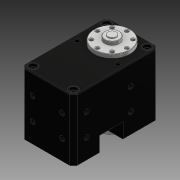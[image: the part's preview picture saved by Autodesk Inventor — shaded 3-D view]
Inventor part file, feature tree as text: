
AUTODESK INVENTOR PART (.ipt)
format: ipt  version: 2016 (Build 200138000, 138)  size: 858,624 bytes
history: native  units: mm
features: other x22, extrude x2, sketch x2
ambient origin geometry x8: Origin, YZ Plane, XZ Plane, XY Plane, X Axis, Y Axis, Z Axis, Center Point
bodies: Body1 (feature_tree), Body2 (feature_tree), Body3 (feature_tree), Body4 (feature_tree), Body5 (feature_tree), Body6 (feature_tree), Body7 (feature_tree), Body8 (feature_tree), Body9 (feature_tree)
feature tree (26):
  other  "<userpath>\Dropbox\Snake\SnakeRobot_normal\cad\parameter_base.xlsx"
  other  "ソリッド1"
  other  "作業平面1"
  extrude  "押し出し1"  Depth=0.5mm
  extrude  "押し出し2"  Depth=10.0mm TaperAngle=0.0deg
  other  "ソリッド2"
  other  "ソリッド3"
  other  "ソリッド4"
  other  "ソリッド5"
  other  "ソリッド6"
  other  "ソリッド7"
  other  "ソリッド8"
  other  "ソリッド9"
  other  "ソリッド10"
  sketch  "スケッチ1"
  sketch  "スケッチ2"
  other  "X-430_IDLE_10:1"
  other  "X-430_SPACER_RING_11:1"
  other  "X-430_SPACER_RING_12:1"
  other  "X-430_SPACER_RING_13:1"
  other  "X-430_SPACER_RING_14:1"
  other  "X-430_SPACER_RING_15:1"
  other  "X-430_SPACER_RING_16:1"
  other  "X-430_SPACER_RING_17:1"
  other  "X-430_SPACER_RING_18:1"
  other  "X-430_CVR_CABLE_19:1"
